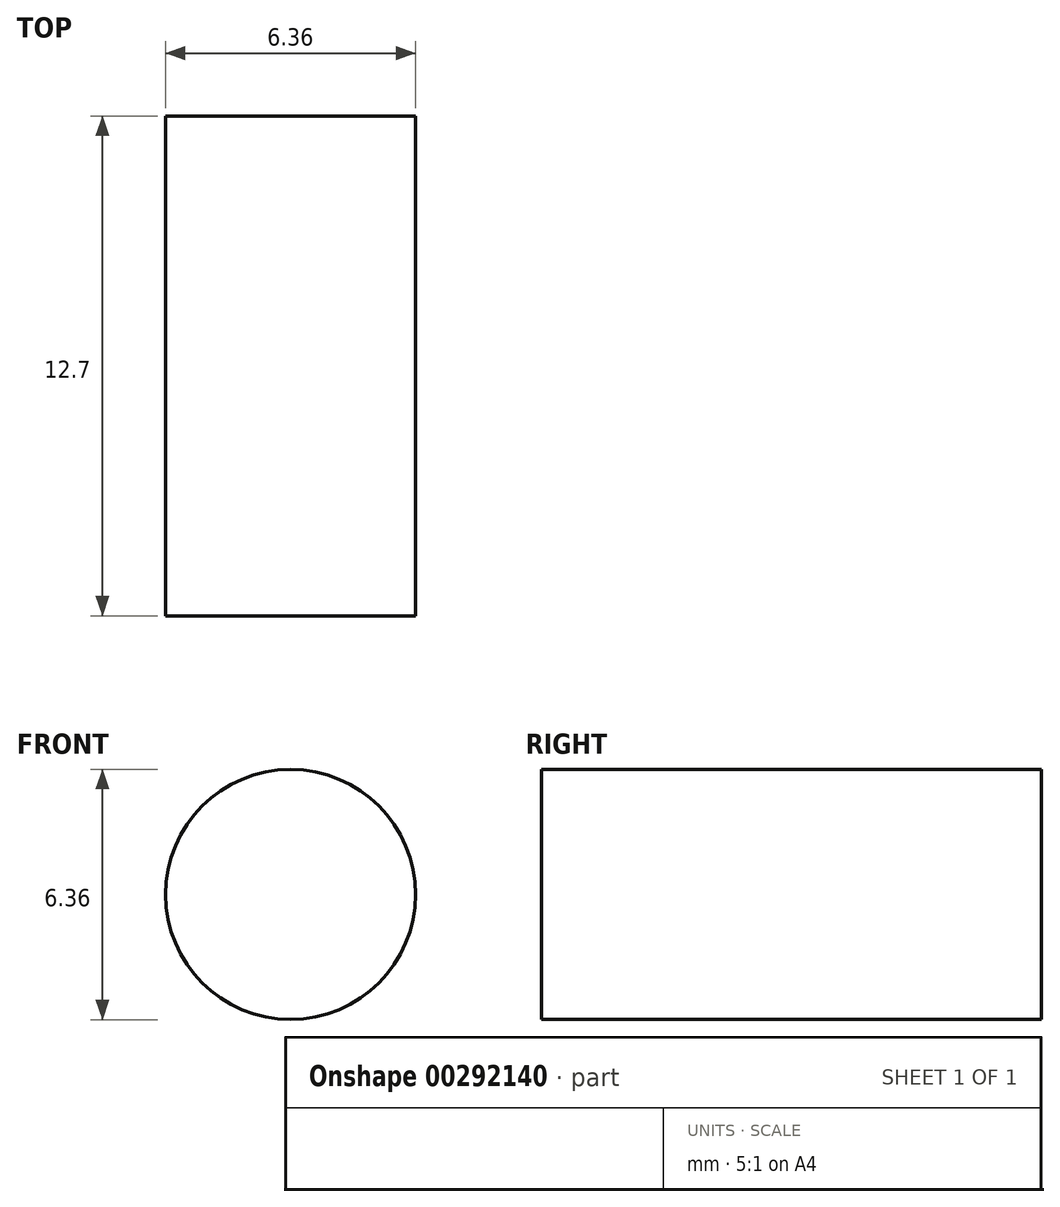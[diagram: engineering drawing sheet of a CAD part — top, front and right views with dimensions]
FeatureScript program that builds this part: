
annotation { "Feature Type Name" : "Feature", "Feature Type Description" : "" }
export const myFeature = defineFeature(function(context is Context, id is Id, definition is map)
    precondition{}
    {
        {
            var Q0;
            Q0=qCreatedBy(makeId("Front.planeOp"),FACE);
            var sketch = newSketch(context, id + "F0", { "sketchPlane" : qUnion([Q0])});
            skCircle(sketch, "E0", {"center": v(0, 0) * mm, "radius": 3.18 * mm});
            skSolve(sketch);
        }
        {
            var Q0;
            Q0 = qSketchRegion(id + "F0", true);
            extrude(context, id + "F1", {"entities" : qUnion([Q0]), "endBound" : BoundingType.SYMMETRIC, "depth" : 12.7 * mm});
        }
    });
